# Revit family: Talos CSD-C02
name_source: partatom
category: Türen
revit_build: Autodesk Revit 2016 (Build: 20150220_1215(x64)
units: mm (PartAtom-declared; Revit-internal decimal feet)

## family parameters
Beim Laden mit Abzugskörper schneiden = Nein
Gemeinsam genutzt = Nein
Immer vertikal = Ja
OmniClass-Nummer = 23.30.10.00
OmniClass-Titel = Doors
Raumberechnungspunkt = Nein

## types (9) — shared parameters
Analytische Konstruktion = <Keine Auswahl>
BaseType = >= 69 mm
CoverMaterial = Glas
Design country = Germany
Dicke = 30 mm  [stored 0.0984252 ft]
Edition number = 1
ElementWeight = 0.00 kg
FrameMaterial = 1.4401 - A4
Funktion = Außen
HandleMaterial = 1.4401 - A4
Hersteller = Kaba GmbH
Konstruktionstyp = Circular Sliding Door
Manufacturer = Kaba GmbH
Manufacturer country = Germany
Manufacturer name = DORMA
Material main = Glass
Material secondary = Metal
Modell = Talos RDR-E01
Nominal height = 2300
OperatingWeight = 0.00 kg
Product SKU = Talos_CSD-C02
RubberMaterial = Zellkautschuk - EPDM
ShutOffDevice = Nein
ShutOffDeviceInside = Nein
Technical description = http://www.kaba.com
Type = Talos CSD-C02
URL = http://www.kaba.com
Weight = 0.00 kg
zero-valued in all types: Nominal width, Weight Net (Kg)

## per-type parameters (varying)
| type | AccessLengthOrRadius | ClearHeight | ConsoleType | CoverWidth | Diameter | DiameterGlassInside | DiameterGlassOutside | DiameterPortal | DiameterSlideDoor | DiameterSlideDoorCover | DiameterSlideDoorFrame | DiameterSlideGlassInside | DiameterSlideGlassOutside | DoorWidth | HasConsoleS1 | HasConsoleS2 | HasMotionSensor | HasShellTopFrame | Height | OuterDiameter | StandardUsed | Width |
| CSD-C02 2000 | 1030 mm | 2100 mm | console : Type 5 | 200 mm  [stored 0.656168 ft] | 1060 mm | 1040 mm  [stored 3.41207 ft] | 1050 mm  [stored 3.44488 ft] | 1070 mm | 970 mm | 1000 mm  [stored 3.28084 ft] | 961 mm | 980 mm  [stored 3.21522 ft] | 990 mm  [stored 3.24803 ft] | 970 mm | Nein | Nein | Nein | Ja | 2300 mm | 2100 mm | Talos CSD-C01-01 | 2100 mm |
| CSD-C02 2200 | 1130 mm | 2200 mm | console : Type 5 | 300 mm | 1160 mm | 1140 mm  [stored 3.74016 ft] | 1150 mm | 1170 mm  [stored 3.83858 ft] | 1070 mm | 1100 mm | 1061 mm | 1080 mm  [stored 3.54331 ft] | 1090 mm  [stored 3.57612 ft] | 1070 mm | Ja | Ja | Ja | Ja | 2500 mm | 2300 mm | Talos CSD-C01-02 | 2300 mm |
| CSD-C02 2400 | 1230 mm  [stored 4.03543 ft] | 2300 mm | console : Type 4 | 200 mm  [stored 0.656168 ft] | 1260 mm  [stored 4.13386 ft] | 1240 mm | 1250 mm  [stored 4.10105 ft] | 1270 mm  [stored 4.16667 ft] | 1170 mm  [stored 3.83858 ft] | 1200 mm  [stored 3.93701 ft] | 1161 mm  [stored 3.80906 ft] | 1180 mm  [stored 3.87139 ft] | 1190 mm  [stored 3.9042 ft] | 1170 mm  [stored 3.83858 ft] | Ja | Ja | Nein | Ja | 2500 mm | 2500 mm | Talos CSD-C01-03 | 2500 mm |
| CSD-C02 2600 | 1330 mm  [stored 4.36352 ft] | 2100 mm | console : Type 5 | 300 mm | 1360 mm  [stored 4.46194 ft] | 1340 mm | 1350 mm  [stored 4.42913 ft] | 1370 mm  [stored 4.49475 ft] | 1270 mm  [stored 4.16667 ft] | 1300 mm  [stored 4.26509 ft] | 1261 mm  [stored 4.13714 ft] | 1280 mm  [stored 4.19948 ft] | 1290 mm | 1270 mm  [stored 4.16667 ft] | Ja | Ja | Ja | Ja | 2400 mm | 2700 mm | Talos CSD-C01-04 | 2700 mm |
| CSD-C02 2800 | 1230 mm  [stored 4.03543 ft] | 2200 mm | console : Type 4 | 200 mm  [stored 0.656168 ft] | 1260 mm  [stored 4.13386 ft] | 1240 mm | 1250 mm  [stored 4.10105 ft] | 1270 mm  [stored 4.16667 ft] | 1170 mm  [stored 3.83858 ft] | 1200 mm  [stored 3.93701 ft] | 1161 mm  [stored 3.80906 ft] | 1180 mm  [stored 3.87139 ft] | 1190 mm  [stored 3.9042 ft] | 1170 mm  [stored 3.83858 ft] | Nein | Nein | Nein | Ja | 2400 mm | 2900 mm | Talos CSD-C01-05 | 2500 mm |
| CSD-C02 3000 | 1530 mm | 2300 mm | console : Type 4 | 300 mm | 1560 mm | 1540 mm | 1550 mm | 1570 mm | 1470 mm | 1500 mm | 1461 mm | 1480 mm | 1490 mm | 1470 mm | Ja | Ja | Ja | Ja | 2600 mm | 3100 mm | Talos CSD-C01-06 | 3100 mm |
| CSD-C02 3200 | 1630 mm | 2100 mm | console : Type 5 | 300 mm | 1660 mm | 1640 mm | 1650 mm | 1670 mm | 1570 mm | 1600 mm | 1561 mm | 1580 mm | 1590 mm | 1570 mm | Ja | Ja | Nein | Ja | 2400 mm | 3300 mm | Talos CSD-C01-07 | 3300 mm |
| CSD-C02 3600 | 1830 mm | 2100 mm | console : Type 4 | 200 mm  [stored 0.656168 ft] | 1860 mm | 1840 mm | 1850 mm | 1870 mm | 1770 mm | 1800 mm | 1761 mm | 1780 mm | 1790 mm | 1770 mm | Ja | Ja | Ja | Nein | 2300 mm | 3700 mm | Talos CSD-C01-09 | 3700 mm |
| CSD-C02 3800 | 1930 mm | 2200 mm | console : Type 5 | 200 mm  [stored 0.656168 ft] | 1960 mm | 1940 mm | 1950 mm | 1970 mm | 1870 mm | 1900 mm | 1861 mm | 1880 mm | 1890 mm | 1870 mm | Ja | Ja | Ja | Ja | 2400 mm | 3900 mm | Talos CSD-C01-10 | 3900 mm |

note: [stored X ft] marks values corroborated as IEEE doubles in the binary element streams (Revit-internal decimal feet)
